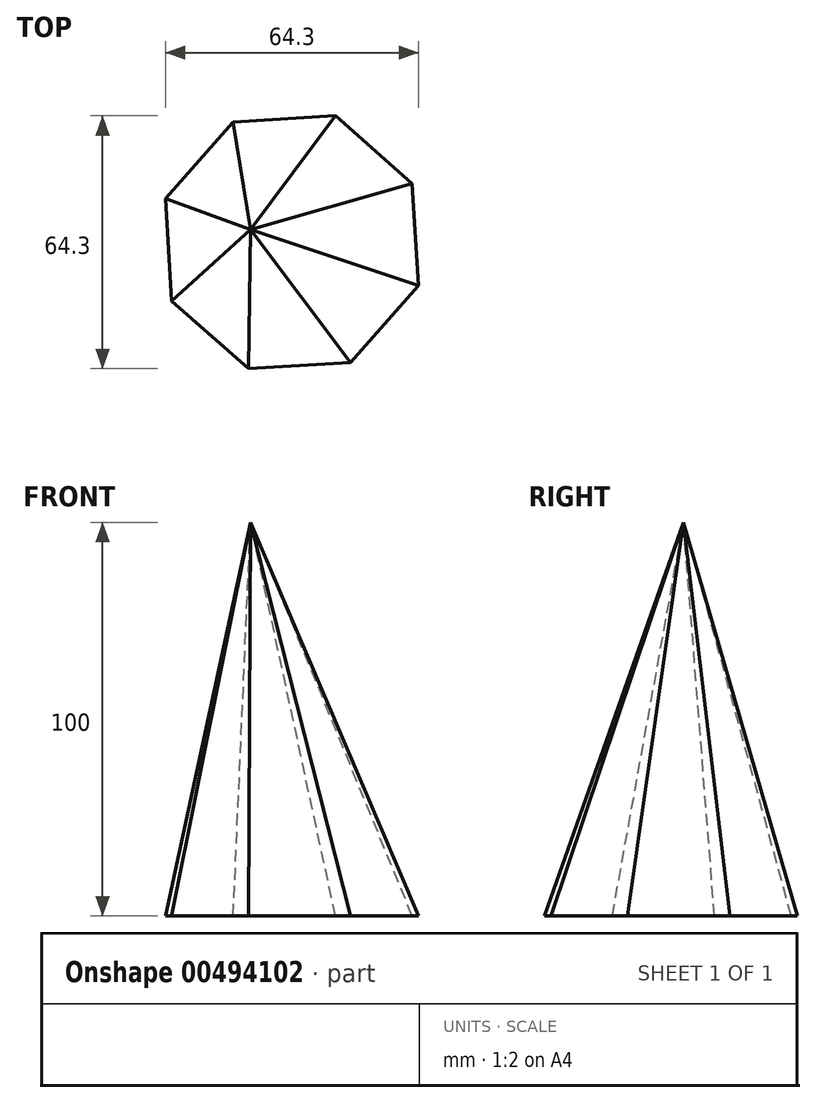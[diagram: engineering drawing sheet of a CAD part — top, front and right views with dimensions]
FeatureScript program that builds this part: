
annotation { "Feature Type Name" : "Feature", "Feature Type Description" : "" }
export const myFeature = defineFeature(function(context is Context, id is Id, definition is map)
    precondition{}
    {
        {
            var Q0;
            Q0=qCreatedBy(makeId("Top.planeOp"),FACE);
            var sketch = newSketch(context, id + "F0", { "sketchPlane" : qUnion([Q0])});
            skCircle(sketch, "E0.cCircle", {"center": v(0, 0) * mm, "radius": 34 * mm, "construction": true});
            skLineSegment(sketch, "E0.0", {"start": v(-14.92, 30.55) * mm, "end": v(11.06, 32.15) * mm});
            skLineSegment(sketch, "E0.1", {"start": v(11.06, 32.15) * mm, "end": v(30.55, 14.92) * mm});
            skLineSegment(sketch, "E0.2", {"start": v(30.55, 14.92) * mm, "end": v(32.15, -11.06) * mm});
            skLineSegment(sketch, "E0.3", {"start": v(32.15, -11.06) * mm, "end": v(14.92, -30.55) * mm});
            skLineSegment(sketch, "E0.4", {"start": v(14.92, -30.55) * mm, "end": v(-11.06, -32.15) * mm});
            skLineSegment(sketch, "E0.5", {"start": v(-11.06, -32.15) * mm, "end": v(-30.55, -14.92) * mm});
            skLineSegment(sketch, "E0.6", {"start": v(-30.55, -14.92) * mm, "end": v(-32.15, 11.06) * mm});
            skLineSegment(sketch, "E0.7", {"start": v(-32.15, 11.06) * mm, "end": v(-14.92, 30.55) * mm});
            skPoint(sketch, "E1", {"position": v(-11.53, -9.1) * mm});
            skSolve(sketch);
        }
        {
            var Q0;
            Q0=qCreatedBy(makeId("Top.planeOp"),FACE);
            cPlane(context, id + "F1", {"entities" : qUnion([Q0]), "cplaneType" : CPlaneType.OFFSET, "offset" : 100 * mm, "width" : 150 * mm, "height" : 150 * mm});
        }
        {
            var Q0;
            Q0=qCreatedBy(id+"F1.planeOp",FACE);
            var sketch = newSketch(context, id + "F2", { "sketchPlane" : qUnion([Q0])});
            skPoint(sketch, "E2", {"position": v(-10.51, 3.18) * mm});
            skSolve(sketch);
        }
        {
            var Q0;
            Q0=makeQuery(id+"F0.imprint","IMPRINT",FACE,{"disambiguationData":[TD([[makeQuery(id+"F0.imprint","IMPRINT",EDGE,{"derivedFrom":sQuery(id+"F0.wireOp",EDGE,"E0.0")}),-1.0]])]});
            var Q1;
            Q1=sQuery(id+"F2.wireOp",VERTEX,"E2");
            loft(context, id + "F3", {"sheetProfilesArray" : [{ "sheetProfileEntities" : qUnion([Q0]) }, { "sheetProfileEntities" : qUnion([Q1]) }]});
        }
    });
